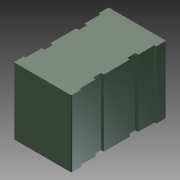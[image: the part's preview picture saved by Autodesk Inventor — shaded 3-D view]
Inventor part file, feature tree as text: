
AUTODESK INVENTOR PART (.ipt)
format: ipt  version: 2014 (Build 180170000, 170)  size: 158,208 bytes
history: native  units: in
note: dims shown in document units (in); Inventor stores cm internally (conversion verified against a paired STEP export)
features: other x21, extrude x3, sketch x3, pattern_linear x1
ambient origin geometry x8: Origin, YZ Plane, XZ Plane, XY Plane, X Axis, Y Axis, Z Axis, Center Point
bodies: Solid1 (feature_tree)
feature tree (28):
  extrude  "Extrusion1"  Depth=0.001in TaperAngle=0.0deg
  extrude  "Extrusion2"  Depth=0.185in TaperAngle=0.0deg
  extrude  "Extrusion3"  [1 undecoded]
  pattern_linear  "Rectangular Pattern1"  [2 undecoded]
  other  "rot_XY"
  other  "rot_YZ"
  other  "rot_ZX"
  other  "rot_X"
  other  "rot_Y"
  other  "rot_Z"
  other  "rot_Center"
  other  "to_cover_XY"
  other  "to_cover_YZ"
  other  "to_cover_ZX"
  other  "to_cover_X"
  other  "to_cover_Y"
  other  "to_cover_Z"
  other  "to_cover_Center"
  other  "to_terminals_XY"
  other  "to_terminals_YZ"
  other  "to_terminals_ZX"
  other  "to_terminals_X"
  other  "to_terminals_Y"
  other  "to_terminals_Z"
  other  "to_terminals_Center"
  sketch  "Sketch_2"  dims[d4=0.01in d5=0.0in d6=0.7874in d8=0.185in d9=0.3937in d11=0.0in]
  sketch  "Sketch_1"  dims[d0=0.361in d1=0.0in d2=0.001in d3=0.0in]
  sketch  "Sketch_7"
note: 3 required parameter values undecoded (feature->parameter linkage not recoverable at this tier; creation-order binding heuristic only, values carry confidence <= 0.55)
